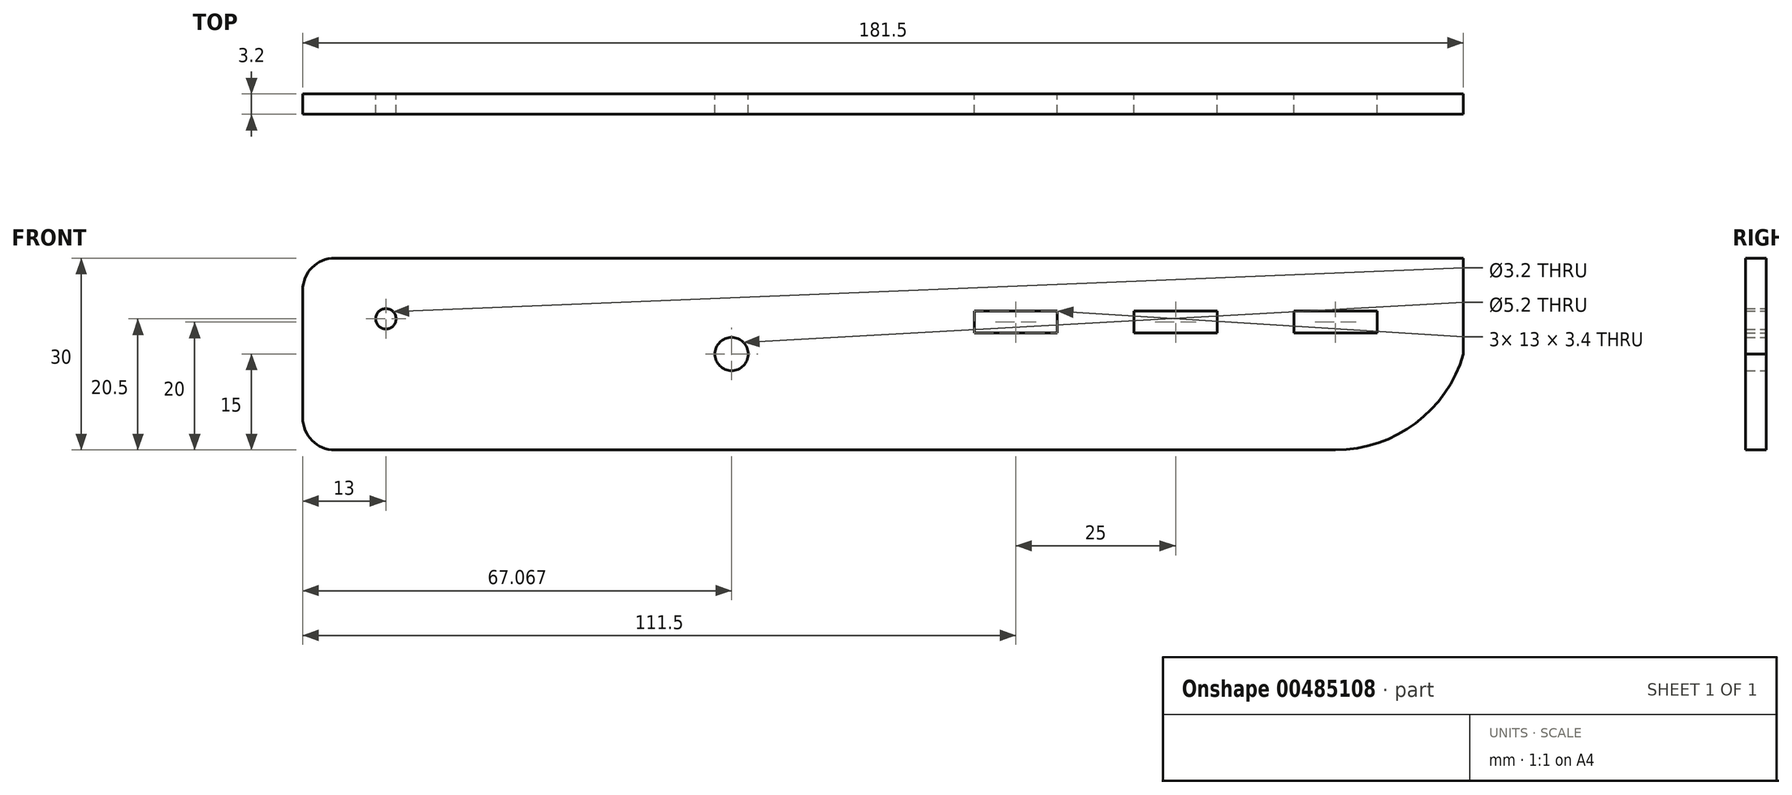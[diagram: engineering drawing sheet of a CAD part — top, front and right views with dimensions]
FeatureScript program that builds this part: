
annotation { "Feature Type Name" : "Feature", "Feature Type Description" : "" }
export const myFeature = defineFeature(function(context is Context, id is Id, definition is map)
    precondition{}
    {
        {
            var Q0;
            Q0=qCreatedBy(makeId("Front.planeOp"),FACE);
            var sketch = newSketch(context, id + "F0", { "sketchPlane" : qUnion([Q0])});
            skLineSegment(sketch, "E0.bottom", {"start": v(-65, 15) * mm, "end": v(65, 15) * mm, "construction": true});
            skLineSegment(sketch, "E0.top", {"start": v(-65, -15) * mm, "end": v(65, -15) * mm, "construction": true});
            skLineSegment(sketch, "E0.left", {"start": v(-65, 15) * mm, "end": v(-65, -15) * mm, "construction": true});
            skLineSegment(sketch, "E0.right", {"start": v(65, 15) * mm, "end": v(65, -15) * mm, "construction": true});
            skPoint(sketch, "E0.middle", {"position": v(0, 0) * mm});
            skLineSegment(sketch, "E1", {"start": v(-65, 0) * mm, "end": v(65, 0) * mm, "construction": true});
            skLineSegment(sketch, "E2", {"start": v(-116.5, 15) * mm, "end": v(-116.5, -15) * mm, "construction": true});
            skLineSegment(sketch, "E3", {"start": v(-116.5, -15) * mm, "end": v(-65, -15) * mm, "construction": true});
            skLineSegment(sketch, "E4", {"start": v(-65, 15) * mm, "end": v(-116.5, 15) * mm, "construction": true});
            skLineSegment(sketch, "E5", {"start": v(-49.43, 15) * mm, "end": v(-49.43, -15) * mm, "construction": true});
            skPoint(sketch, "E6", {"position": v(-49.43, 0) * mm});
            skCircle(sketch, "E7", {"center": v(-49.43, 0) * mm, "radius": 2.6 * mm});
            skLineSegment(sketch, "E8", {"start": v(-65, 5) * mm, "end": v(65, 5) * mm, "construction": true});
            skLineSegment(sketch, "E9", {"start": v(45, 15) * mm, "end": v(45, -15) * mm, "construction": true});
            skLineSegment(sketch, "E10", {"start": v(20, 15) * mm, "end": v(20, -15) * mm, "construction": true});
            skLineSegment(sketch, "E11", {"start": v(-5, 15) * mm, "end": v(-5, -15) * mm, "construction": true});
            skPoint(sketch, "E12", {"position": v(-5, 5) * mm});
            skPoint(sketch, "E13", {"position": v(20, 5) * mm});
            skPoint(sketch, "E14", {"position": v(45, 5) * mm});
            skLineSegment(sketch, "E15.bottom", {"start": v(1.5, 6.7) * mm, "end": v(-11.5, 6.7) * mm});
            skLineSegment(sketch, "E15.top", {"start": v(1.5, 3.3) * mm, "end": v(-11.5, 3.3) * mm});
            skLineSegment(sketch, "E15.left", {"start": v(1.5, 6.7) * mm, "end": v(1.5, 3.3) * mm});
            skLineSegment(sketch, "E15.right", {"start": v(-11.5, 6.7) * mm, "end": v(-11.5, 3.3) * mm});
            skLineSegment(sketch, "E16", {"start": v(1.5, 6.7) * mm, "end": v(65, 6.7) * mm, "construction": true});
            skLineSegment(sketch, "E17", {"start": v(1.5, 3.3) * mm, "end": v(65, 3.3) * mm, "construction": true});
            skLineSegment(sketch, "E18", {"start": v(13.5, 6.7) * mm, "end": v(13.5, 3.3) * mm, "construction": true});
            skLineSegment(sketch, "E19", {"start": v(26.5, 6.7) * mm, "end": v(26.5, 3.3) * mm, "construction": true});
            skLineSegment(sketch, "E20", {"start": v(38.5, 6.7) * mm, "end": v(38.5, 3.3) * mm, "construction": true});
            skLineSegment(sketch, "E21", {"start": v(51.5, 6.7) * mm, "end": v(51.5, 3.3) * mm, "construction": true});
            skLineSegment(sketch, "E22", {"start": v(13.5, 6.7) * mm, "end": v(26.5, 6.7) * mm});
            skLineSegment(sketch, "E23", {"start": v(13.5, 3.3) * mm, "end": v(26.5, 3.3) * mm});
            skLineSegment(sketch, "E24", {"start": v(38.5, 3.3) * mm, "end": v(51.5, 3.3) * mm});
            skLineSegment(sketch, "E25", {"start": v(38.5, 6.7) * mm, "end": v(51.5, 6.7) * mm});
            skLineSegment(sketch, "E26", {"start": v(51.5, 6.7) * mm, "end": v(51.5, 3.3) * mm});
            skLineSegment(sketch, "E27", {"start": v(38.5, 6.7) * mm, "end": v(38.5, 3.3) * mm});
            skLineSegment(sketch, "E28", {"start": v(26.5, 6.7) * mm, "end": v(26.5, 3.3) * mm});
            skLineSegment(sketch, "E29", {"start": v(13.5, 6.7) * mm, "end": v(13.5, 3.3) * mm});
            skLineSegment(sketch, "E30", {"start": v(-116.5, 15) * mm, "end": v(-65, 15) * mm});
            skLineSegment(sketch, "E31", {"start": v(-65, 15) * mm, "end": v(65, 15) * mm});
            skLineSegment(sketch, "E32", {"start": v(-65, -15) * mm, "end": v(-116.5, -15) * mm});
            skLineSegment(sketch, "E33", {"start": v(-116.5, -15) * mm, "end": v(-116.5, 15) * mm});
            skLineSegment(sketch, "E34", {"start": v(-65, -15) * mm, "end": v(45, -15) * mm});
            skArc(sketch, "E35", {"start": v(45, -15) * mm, "mid": v(57.5, -10.83) * mm, "end": v(65, 0) * mm});
            skLineSegment(sketch, "E36", {"start": v(65, 15) * mm, "end": v(65, 0) * mm});
            skLineSegment(sketch, "E37", {"start": v(-103.5, 15.1) * mm, "end": v(-103.5, -15) * mm, "construction": true});
            skLineSegment(sketch, "E38", {"start": v(-116.5, 5.5) * mm, "end": v(-65, 5.5) * mm, "construction": true});
            skCircle(sketch, "E39", {"center": v(-103.5, 5.5) * mm, "radius": 1.6 * mm});
            skSolve(sketch);
        }
        {
            var Q0;
            Q0=makeQuery(id+"F0.imprint","IMPRINT",FACE,{"disambiguationData":[TD([[makeQuery(id+"F0.imprint","IMPRINT",EDGE,{"derivedFrom":sQuery(id+"F0.wireOp",EDGE,"E7")}),-1.0]])]});
            extrude(context, id + "F1", {"entities" : qUnion([Q0]), "depth" : 3.2 * mm, "offsetDistance" : 25 * mm});
        }
        {
            var Q0;
            Q0=makeQuery(id+"F1.opExtrude","SWEPT_EDGE",EDGE,{"disambiguationData":[OSD([sQuery(id+"F0.wireOp",EDGE,"E30"),sQuery(id+"F0.wireOp",EDGE,"E33")])]});
            var Q1;
            Q1=makeQuery(id+"F1.opExtrude","SWEPT_EDGE",EDGE,{"disambiguationData":[OSD([sQuery(id+"F0.wireOp",EDGE,"E32"),sQuery(id+"F0.wireOp",EDGE,"E33")])]});
            fillet(context, id + "F2", {"entities" : qUnion([Q0, Q1]), "radius" : 5 * mm, "tangentPropagation" : true, "allowEdgeOverflow" : false});
        }
    });
